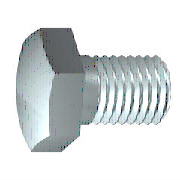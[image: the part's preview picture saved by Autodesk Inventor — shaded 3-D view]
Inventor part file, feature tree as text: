
AUTODESK INVENTOR PART (.ipt)
format: ipt  version: 2013 (Build 170138000, 138)  size: 185,856 bytes
history: native  units: mm (DEFAULTED — no unit token found)
features: sketch x2, extrude x1, chamfer x1, plane x1
ambient origin geometry x7: Origin, YZ Plane, XZ Plane, X Axis, Y Axis, Z Axis, Center Point
bodies: Solid1 (feature_tree), Body (feature_tree)
feature tree (5):
  extrude  "Head"  TaperAngle=90.0deg  [1 undecoded]
  chamfer  "Chamfer1"  [1 undecoded]
  plane  "Work Plane1"
  sketch  "Sketch1"  dims[d2=8.0mm d12=90.0deg]
  sketch  "Sketch2"  dims[d3=5.68mm d4=0.0mm d21=90.0deg d6=0.766813mm d7=0.766912mm d8=0.0mm d11=13.0mm d15=22.0mm d16=0.0mm d55=45.0deg d58=0.0mm d59=40.0mm d65=13.0mm d67=30.0deg d68=15.6mm d69=5.68mm d71=0.1mm d73=0.0mm]
note: 2 required parameter values undecoded (feature->parameter linkage not recoverable at this tier; creation-order binding heuristic only, values carry confidence <= 0.55)
